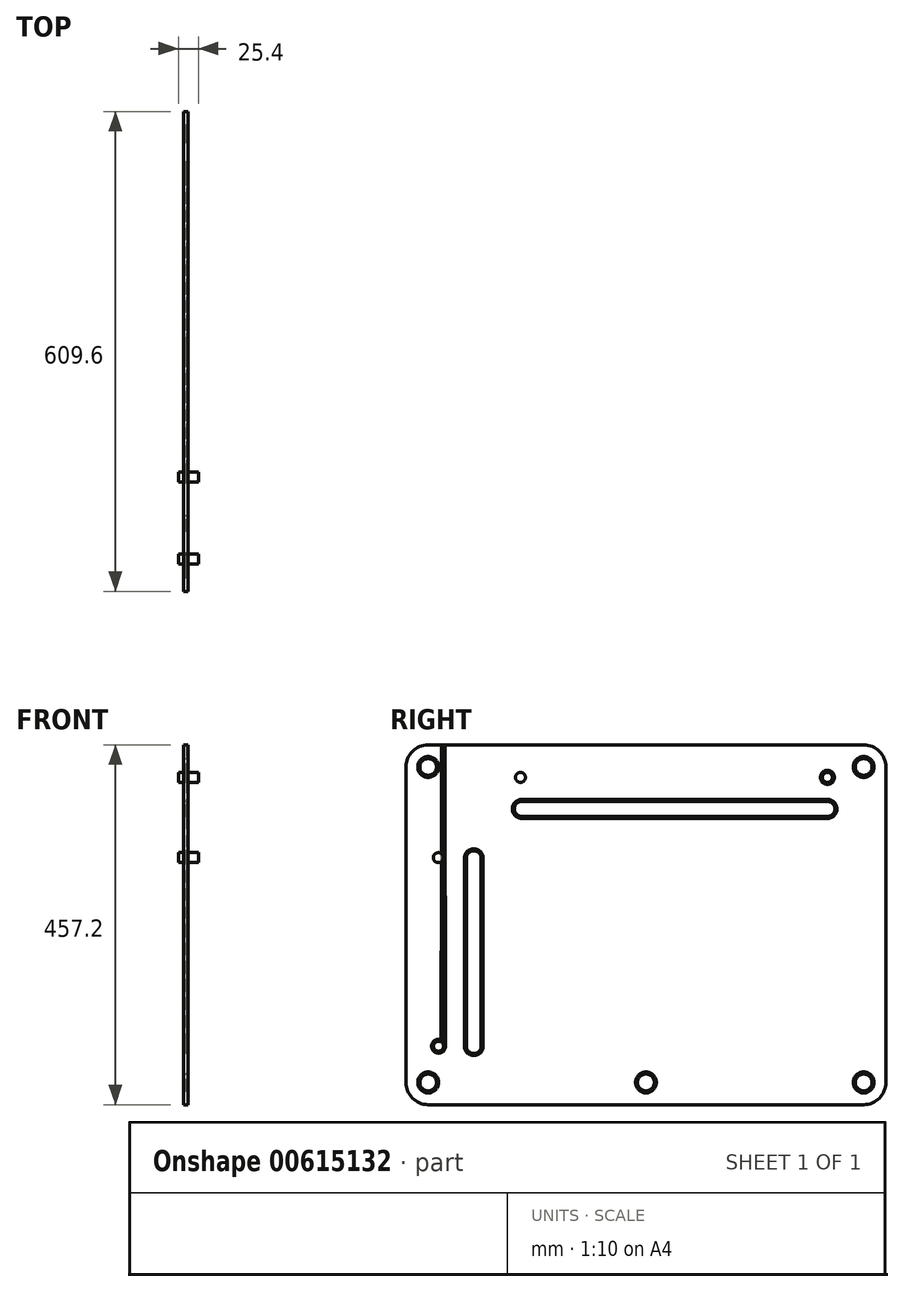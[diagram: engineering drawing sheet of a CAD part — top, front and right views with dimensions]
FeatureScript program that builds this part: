
annotation { "Feature Type Name" : "Feature", "Feature Type Description" : "" }
export const myFeature = defineFeature(function(context is Context, id is Id, definition is map)
    precondition{}
    {
        {
            var Q0;
            Q0=qCreatedBy(makeId("Right.planeOp"),FACE);
            var sketch = newSketch(context, id + "F0", { "sketchPlane" : qUnion([Q0])});
            skPoint(sketch, "E0.middle", {"position": v(0, 0) * mm});
            skLineSegment(sketch, "E1.bottom", {"start": v(304.8, -228.6) * mm, "end": v(-304.8, -228.6) * mm});
            skLineSegment(sketch, "E1.top", {"start": v(304.8, 228.6) * mm, "end": v(-304.8, 228.6) * mm});
            skLineSegment(sketch, "E1.left", {"start": v(304.8, -228.6) * mm, "end": v(304.8, 228.6) * mm});
            skLineSegment(sketch, "E1.right", {"start": v(-304.8, -228.6) * mm, "end": v(-304.8, 228.6) * mm});
            skSolve(sketch);
        }
        {
            var Q0;
            Q0=makeQuery(id+"F0.imprint","IMPRINT",FACE,{"disambiguationData":[TD([[makeQuery(id+"F0.imprint","IMPRINT",EDGE,{"derivedFrom":sQuery(id+"F0.wireOp",EDGE,"E1.bottom")}),-1.0]])]});
            extrude(context, id + "F1", {"entities" : qUnion([Q0]), "depth" : 6.35 * mm, "offsetDistance" : 25.4 * mm});
        }
        {
            var Q0;
            Q0=makeQuery(id+"F1.opExtrude","SWEPT_EDGE",EDGE,{"disambiguationData":[OSD([sQuery(id+"F0.wireOp",EDGE,"E1.top"),sQuery(id+"F0.wireOp",EDGE,"E1.right")])]});
            var Q1;
            Q1=makeQuery(id+"F1.opExtrude","SWEPT_EDGE",EDGE,{"disambiguationData":[OSD([sQuery(id+"F0.wireOp",EDGE,"E1.top"),sQuery(id+"F0.wireOp",EDGE,"E1.left")])]});
            var Q2;
            Q2=makeQuery(id+"F1.opExtrude","SWEPT_EDGE",EDGE,{"disambiguationData":[OSD([sQuery(id+"F0.wireOp",EDGE,"E1.bottom"),sQuery(id+"F0.wireOp",EDGE,"E1.right")])]});
            var Q3;
            Q3=makeQuery(id+"F1.opExtrude","SWEPT_EDGE",EDGE,{"disambiguationData":[OSD([sQuery(id+"F0.wireOp",EDGE,"E1.bottom"),sQuery(id+"F0.wireOp",EDGE,"E1.left")])]});
            fillet(context, id + "F2", {"entities" : qUnion([Q0, Q1, Q2, Q3]), "radius" : 28.2 * mm, "tangentPropagation" : true, "allowEdgeOverflow" : false});
        }
        {
            var Q0;
            Q0=makeQuery(id+"F1.opExtrude","CAP_FACE",FACE,{"disambiguationData":[OSD([sQuery(id+"F0.wireOp",EDGE,"E1.bottom"),sQuery(id+"F0.wireOp",EDGE,"E1.top"),sQuery(id+"F0.wireOp",EDGE,"E1.left"),sQuery(id+"F0.wireOp",EDGE,"E1.right")])],"isStart":true});
            var sketch = newSketch(context, id + "F3", { "sketchPlane" : qUnion([Q0])});
            skCircle(sketch, "E2", {"center": v(276.6, 200.4) * mm, "radius": 10.67 * mm});
            skCircle(sketch, "E3.MirrorC", {"center": v(-276.6, 200.4) * mm, "radius": 10.67 * mm});
            skCircle(sketch, "E4.MirrorC", {"center": v(276.6, -200.4) * mm, "radius": 10.67 * mm});
            skCircle(sketch, "E5.MirrorC", {"center": v(-276.6, -200.4) * mm, "radius": 10.67 * mm});
            skCircle(sketch, "E6", {"center": v(0, -200.4) * mm, "radius": 10.67 * mm});
            skSolve(sketch);
        }
        {
            var Q0;
            Q0 = qSketchRegion(id + "F3", true);
            extrude(context, id + "F4", {"entities" : qUnion([Q0]), "endBound" : BoundingType.SYMMETRIC, "depth" : 25.4 * mm, "offsetDistance" : 25.4 * mm});
        }
        {
            var Q0;
            Q0=makeQuery(id+"F4.opExtrude","SWEPT_BODY",BODY,{"disambiguationData":[OSD([sQuery(id+"F3.wireOp",EDGE,"E2")])]});
            var Q1;
            Q1=makeQuery(id+"F4.opExtrude","SWEPT_BODY",BODY,{"disambiguationData":[OSD([sQuery(id+"F3.wireOp",EDGE,"E3.MirrorC")])]});
            var Q2;
            Q2=makeQuery(id+"F4.opExtrude","SWEPT_BODY",BODY,{"disambiguationData":[OSD([sQuery(id+"F3.wireOp",EDGE,"E5.MirrorC")])]});
            var Q3;
            Q3=makeQuery(id+"F4.opExtrude","SWEPT_BODY",BODY,{"disambiguationData":[OSD([sQuery(id+"F3.wireOp",EDGE,"E6")])]});
            var Q4;
            Q4=makeQuery(id+"F4.opExtrude","SWEPT_BODY",BODY,{"disambiguationData":[OSD([sQuery(id+"F3.wireOp",EDGE,"E4.MirrorC")])]});
            var Q5;
            Q5=makeQuery(id+"F1.opExtrude","SWEPT_BODY",BODY,{"disambiguationData":[OSD([sQuery(id+"F0.wireOp",EDGE,"E1.bottom"),sQuery(id+"F0.wireOp",EDGE,"E1.top"),sQuery(id+"F0.wireOp",EDGE,"E1.left"),sQuery(id+"F0.wireOp",EDGE,"E1.right")])]});
            var Q6;
            Q6=makeQuery(id+"F1.opExtrude","SWEPT_BODY",BODY,{"disambiguationData":[OSD([sQuery(id+"F0.wireOp",EDGE,"E1.bottom"),sQuery(id+"F0.wireOp",EDGE,"E1.top"),sQuery(id+"F0.wireOp",EDGE,"E1.left"),sQuery(id+"F0.wireOp",EDGE,"E1.right")])]});
            booleanBodies(context, id + "F5", {"operationType" : BooleanOperationType.SUBTRACTION, "tools" : qUnion([Q0, Q1, Q2, Q3, Q4]), "targets" : qUnion([Q5, Q6])});
        }
        {
            var Q0;
            Q0=makeQuery(id+"F5.opBoolean","INTERSECT",EDGE,{"derivedFrom":[makeQuery(id+"F1.opExtrude","CAP_FACE",FACE,{"disambiguationData":[OSD([sQuery(id+"F0.wireOp",EDGE,"E1.bottom"),sQuery(id+"F0.wireOp",EDGE,"E1.top"),sQuery(id+"F0.wireOp",EDGE,"E1.left"),sQuery(id+"F0.wireOp",EDGE,"E1.right")])],"isStart":false}),makeQuery(id+"F4.opExtrude","SWEPT_FACE",FACE,{"disambiguationData":[OSD([sQuery(id+"F3.wireOp",EDGE,"E2")])]})]});
            var Q1;
            Q1=makeQuery(id+"F5.opBoolean","INTERSECT",EDGE,{"derivedFrom":[makeQuery(id+"F1.opExtrude","CAP_FACE",FACE,{"disambiguationData":[OSD([sQuery(id+"F0.wireOp",EDGE,"E1.bottom"),sQuery(id+"F0.wireOp",EDGE,"E1.top"),sQuery(id+"F0.wireOp",EDGE,"E1.left"),sQuery(id+"F0.wireOp",EDGE,"E1.right")])],"isStart":false}),makeQuery(id+"F4.opExtrude","SWEPT_FACE",FACE,{"disambiguationData":[OSD([sQuery(id+"F3.wireOp",EDGE,"E3.MirrorC")])]})]});
            var Q2;
            Q2=makeQuery(id+"F5.opBoolean","INTERSECT",EDGE,{"derivedFrom":[makeQuery(id+"F1.opExtrude","CAP_FACE",FACE,{"disambiguationData":[OSD([sQuery(id+"F0.wireOp",EDGE,"E1.bottom"),sQuery(id+"F0.wireOp",EDGE,"E1.top"),sQuery(id+"F0.wireOp",EDGE,"E1.left"),sQuery(id+"F0.wireOp",EDGE,"E1.right")])],"isStart":false}),makeQuery(id+"F4.opExtrude","SWEPT_FACE",FACE,{"disambiguationData":[OSD([sQuery(id+"F3.wireOp",EDGE,"E6")])]})]});
            var Q3;
            Q3=makeQuery(id+"F5.opBoolean","INTERSECT",EDGE,{"derivedFrom":[makeQuery(id+"F1.opExtrude","CAP_FACE",FACE,{"disambiguationData":[OSD([sQuery(id+"F0.wireOp",EDGE,"E1.bottom"),sQuery(id+"F0.wireOp",EDGE,"E1.top"),sQuery(id+"F0.wireOp",EDGE,"E1.left"),sQuery(id+"F0.wireOp",EDGE,"E1.right")])],"isStart":false}),makeQuery(id+"F4.opExtrude","SWEPT_FACE",FACE,{"disambiguationData":[OSD([sQuery(id+"F3.wireOp",EDGE,"E5.MirrorC")])]})]});
            var Q4;
            Q4=makeQuery(id+"F5.opBoolean","INTERSECT",EDGE,{"derivedFrom":[makeQuery(id+"F1.opExtrude","CAP_FACE",FACE,{"disambiguationData":[OSD([sQuery(id+"F0.wireOp",EDGE,"E1.bottom"),sQuery(id+"F0.wireOp",EDGE,"E1.top"),sQuery(id+"F0.wireOp",EDGE,"E1.left"),sQuery(id+"F0.wireOp",EDGE,"E1.right")])],"isStart":false}),makeQuery(id+"F4.opExtrude","SWEPT_FACE",FACE,{"disambiguationData":[OSD([sQuery(id+"F3.wireOp",EDGE,"E4.MirrorC")])]})]});
            chamfer(context, id + "F6", {"entities" : qUnion([Q0, Q1, Q2, Q3, Q4]), "width" : 2.54 * mm, "tangentPropagation" : true});
        }
        {
            var Q0;
            Q0=makeQuery(id+"F1.opExtrude","CAP_FACE",FACE,{"disambiguationData":[OSD([sQuery(id+"F0.wireOp",EDGE,"E1.bottom"),sQuery(id+"F0.wireOp",EDGE,"E1.top"),sQuery(id+"F0.wireOp",EDGE,"E1.left"),sQuery(id+"F0.wireOp",EDGE,"E1.right")])],"isStart":false});
            var sketch = newSketch(context, id + "F7", { "sketchPlane" : qUnion([Q0])});
            skSolve(sketch);
        }
        {
            var Q0;
            Q0=makeQuery(id+"F1.opExtrude","CAP_FACE",FACE,{"disambiguationData":[OSD([sQuery(id+"F0.wireOp",EDGE,"E1.bottom"),sQuery(id+"F0.wireOp",EDGE,"E1.top"),sQuery(id+"F0.wireOp",EDGE,"E1.left"),sQuery(id+"F0.wireOp",EDGE,"E1.right")])],"isStart":false});
            var sketch = newSketch(context, id + "F8", { "sketchPlane" : qUnion([Q0])});
            skLineSegment(sketch, "E7", {"start": v(-230.16, 193.53) * mm, "end": v(117.73, 193.53) * mm});
            skLineSegment(sketch, "E8", {"start": v(-230.5, 180.84) * mm, "end": v(159.64, 180.84) * mm});
            skLineSegment(sketch, "E9.MirrorCS", {"start": v(-257.1, 154.28) * mm, "end": v(-257.64, -235.87) * mm});
            skLineSegment(sketch, "E10.MirrorCS", {"start": v(-269.8, 153.95) * mm, "end": v(-270.27, -193.94) * mm});
            skLineSegment(sketch, "E11.MirrorCS", {"start": v(230.5, 180.84) * mm, "end": v(-159.64, 180.84) * mm});
            skLineSegment(sketch, "E12.MirrorCS", {"start": v(230.16, 193.53) * mm, "end": v(-117.73, 193.53) * mm});
            skCircle(sketch, "E13.MirrorC", {"center": v(230.5, 187.2) * mm, "radius": 6.35 * mm});
            skCircle(sketch, "E14.MirrorC", {"center": v(-263.45, -154.29) * mm, "radius": 6.35 * mm});
            skLineSegment(sketch, "E15.MirrorCS", {"start": v(-257.1, -154.28) * mm, "end": v(-257.64, 235.87) * mm});
            skLineSegment(sketch, "E16.MirrorCS", {"start": v(-269.8, -153.95) * mm, "end": v(-270.27, 193.94) * mm});
            skCircle(sketch, "E17", {"center": v(-159.4, 187.19) * mm, "radius": 6.35 * mm});
            skPoint(sketch, "E17.second.point", {"position": v(-159.64, 193.53) * mm});
            skPoint(sketch, "E17.third.point", {"position": v(-165.6, 185.8) * mm});
            skPoint(sketch, "E18.first.point", {"position": v(-270.12, 81.94) * mm});
            skPoint(sketch, "E18.second.point", {"position": v(-257.43, 81.94) * mm});
            skPoint(sketch, "E18.third.point", {"position": v(-257.43, 81.39) * mm});
            skCircle(sketch, "E19", {"center": v(-263.77, 85.22) * mm, "radius": 6.35 * mm});
            skPoint(sketch, "E19.first.point", {"position": v(-257.43, 85.64) * mm});
            skPoint(sketch, "E19.second.point", {"position": v(-270.12, 85.12) * mm});
            skPoint(sketch, "E19.third.point", {"position": v(-262.85, 78.93) * mm});
            skSolve(sketch);
        }
        {
            var Q0;
            Q0 = qSketchRegion(id + "F8", true);
            extrude(context, id + "F9", {"entities" : qUnion([Q0]), "endBound" : BoundingType.SYMMETRIC, "depth" : 25.4 * mm, "offsetDistance" : 25.4 * mm});
        }
        {
            var Q0;
            Q0=makeQuery(id+"F9.opExtrude","SWEPT_BODY",BODY,{"disambiguationData":[OSD([sQuery(id+"F8.wireOp",EDGE,"JYx8LGtQ-4H3j-zVlU-k91Q-ysmHY4vAFXg0"),sQuery(id+"F8.wireOp",EDGE,"E7"),sQuery(id+"F8.wireOp",EDGE,"E8"),sQuery(id+"F8.wireOp",EDGE,"E11.MirrorCS"),sQuery(id+"F8.wireOp",EDGE,"E12.MirrorCS"),sQuery(id+"F8.wireOp",EDGE,"E13.MirrorC")])]});
            var Q1;
            Q1=makeQuery(id+"F9.opExtrude","SWEPT_BODY",BODY,{"disambiguationData":[OSD([sQuery(id+"F8.wireOp",EDGE,"E9.MirrorCS"),sQuery(id+"F8.wireOp",EDGE,"2af65969-cf82-4882-8e88-bc3bc080c73c0.MirrorC"),sQuery(id+"F8.wireOp",EDGE,"E10.MirrorCS"),sQuery(id+"F8.wireOp",EDGE,"E14.MirrorC"),sQuery(id+"F8.wireOp",EDGE,"E16.MirrorCS"),sQuery(id+"F8.wireOp",EDGE,"E15.MirrorCS")])]});
            var Q2;
            Q2=makeQuery(id+"F1.opExtrude","SWEPT_BODY",BODY,{"disambiguationData":[OSD([sQuery(id+"F0.wireOp",EDGE,"E1.bottom"),sQuery(id+"F0.wireOp",EDGE,"E1.top"),sQuery(id+"F0.wireOp",EDGE,"E1.left"),sQuery(id+"F0.wireOp",EDGE,"E1.right")])]});
            booleanBodies(context, id + "F10", {"operationType" : BooleanOperationType.SUBTRACTION, "tools" : qUnion([Q0, Q1]), "targets" : qUnion([Q2])});
        }
        {
            var Q0;
            Q0=makeQuery(id+"F10.opBoolean","INTERSECT",EDGE,{"derivedFrom":[makeQuery(id+"F1.opExtrude","CAP_FACE",FACE,{"disambiguationData":[OSD([sQuery(id+"F0.wireOp",EDGE,"E1.bottom"),sQuery(id+"F0.wireOp",EDGE,"E1.top"),sQuery(id+"F0.wireOp",EDGE,"E1.left"),sQuery(id+"F0.wireOp",EDGE,"E1.right")])],"isStart":false}),makeQuery(id+"F9.opExtrude","SWEPT_FACE",FACE,{"disambiguationData":[OSD([sQuery(id+"F8.wireOp",EDGE,"E16.MirrorCS")])]})]});
            var Q1;
            Q1=makeQuery(id+"F10.opBoolean","INTERSECT",EDGE,{"derivedFrom":[makeQuery(id+"F1.opExtrude","CAP_FACE",FACE,{"disambiguationData":[OSD([sQuery(id+"F0.wireOp",EDGE,"E1.bottom"),sQuery(id+"F0.wireOp",EDGE,"E1.top"),sQuery(id+"F0.wireOp",EDGE,"E1.left"),sQuery(id+"F0.wireOp",EDGE,"E1.right")])],"isStart":false}),makeQuery(id+"F9.opExtrude","SWEPT_FACE",FACE,{"disambiguationData":[OSD([sQuery(id+"F8.wireOp",EDGE,"E10.MirrorCS")])]})]});
            var Q2;
            Q2=makeQuery(id+"F10.opBoolean","INTERSECT",EDGE,{"derivedFrom":[makeQuery(id+"F1.opExtrude","CAP_FACE",FACE,{"disambiguationData":[OSD([sQuery(id+"F0.wireOp",EDGE,"E1.bottom"),sQuery(id+"F0.wireOp",EDGE,"E1.top"),sQuery(id+"F0.wireOp",EDGE,"E1.left"),sQuery(id+"F0.wireOp",EDGE,"E1.right")])],"isStart":false}),makeQuery(id+"F9.opExtrude","SWEPT_FACE",FACE,{"disambiguationData":[OSD([sQuery(id+"F8.wireOp",EDGE,"E15.MirrorCS")])]})]});
            var Q3;
            Q3=makeQuery(id+"F10.opBoolean","INTERSECT",EDGE,{"derivedFrom":[makeQuery(id+"F1.opExtrude","CAP_FACE",FACE,{"disambiguationData":[OSD([sQuery(id+"F0.wireOp",EDGE,"E1.bottom"),sQuery(id+"F0.wireOp",EDGE,"E1.top"),sQuery(id+"F0.wireOp",EDGE,"E1.left"),sQuery(id+"F0.wireOp",EDGE,"E1.right")])],"isStart":false}),makeQuery(id+"F9.opExtrude","SWEPT_FACE",FACE,{"disambiguationData":[OSD([sQuery(id+"F8.wireOp",EDGE,"E9.MirrorCS")])]})]});
            var Q4;
            Q4=makeQuery(id+"F10.opBoolean","INTERSECT",EDGE,{"derivedFrom":[makeQuery(id+"F1.opExtrude","CAP_FACE",FACE,{"disambiguationData":[OSD([sQuery(id+"F0.wireOp",EDGE,"E1.bottom"),sQuery(id+"F0.wireOp",EDGE,"E1.top"),sQuery(id+"F0.wireOp",EDGE,"E1.left"),sQuery(id+"F0.wireOp",EDGE,"E1.right")])],"isStart":false}),makeQuery(id+"F9.opExtrude","SWEPT_FACE",FACE,{"disambiguationData":[OSD([sQuery(id+"F8.wireOp",EDGE,"E14.MirrorC")])]})]});
            var Q5;
            Q5=makeQuery(id+"F10.opBoolean","INTERSECT",EDGE,{"derivedFrom":[makeQuery(id+"F1.opExtrude","CAP_FACE",FACE,{"disambiguationData":[OSD([sQuery(id+"F0.wireOp",EDGE,"E1.bottom"),sQuery(id+"F0.wireOp",EDGE,"E1.top"),sQuery(id+"F0.wireOp",EDGE,"E1.left"),sQuery(id+"F0.wireOp",EDGE,"E1.right")])],"isStart":false}),makeQuery(id+"F9.opExtrude","SWEPT_FACE",FACE,{"disambiguationData":[OSD([sQuery(id+"F8.wireOp",EDGE,"2af65969-cf82-4882-8e88-bc3bc080c73c0.MirrorC")])]})]});
            var Q6;
            Q6=makeQuery(id+"F10.opBoolean","INTERSECT",EDGE,{"derivedFrom":[makeQuery(id+"F1.opExtrude","CAP_FACE",FACE,{"disambiguationData":[OSD([sQuery(id+"F0.wireOp",EDGE,"E1.bottom"),sQuery(id+"F0.wireOp",EDGE,"E1.top"),sQuery(id+"F0.wireOp",EDGE,"E1.left"),sQuery(id+"F0.wireOp",EDGE,"E1.right")])],"isStart":false}),makeQuery(id+"F9.opExtrude","SWEPT_FACE",FACE,{"disambiguationData":[OSD([sQuery(id+"F8.wireOp",EDGE,"E8"),sQuery(id+"F8.wireOp",EDGE,"E11.MirrorCS")])]})]});
            var Q7;
            Q7=makeQuery(id+"F10.opBoolean","INTERSECT",EDGE,{"derivedFrom":[makeQuery(id+"F1.opExtrude","CAP_FACE",FACE,{"disambiguationData":[OSD([sQuery(id+"F0.wireOp",EDGE,"E1.bottom"),sQuery(id+"F0.wireOp",EDGE,"E1.top"),sQuery(id+"F0.wireOp",EDGE,"E1.left"),sQuery(id+"F0.wireOp",EDGE,"E1.right")])],"isStart":false}),makeQuery(id+"F9.opExtrude","SWEPT_FACE",FACE,{"disambiguationData":[OSD([sQuery(id+"F8.wireOp",EDGE,"E7"),sQuery(id+"F8.wireOp",EDGE,"E12.MirrorCS")])]})]});
            var Q8;
            Q8=makeQuery(id+"F10.opBoolean","INTERSECT",EDGE,{"derivedFrom":[makeQuery(id+"F1.opExtrude","CAP_FACE",FACE,{"disambiguationData":[OSD([sQuery(id+"F0.wireOp",EDGE,"E1.bottom"),sQuery(id+"F0.wireOp",EDGE,"E1.top"),sQuery(id+"F0.wireOp",EDGE,"E1.left"),sQuery(id+"F0.wireOp",EDGE,"E1.right")])],"isStart":false}),makeQuery(id+"F9.opExtrude","SWEPT_FACE",FACE,{"disambiguationData":[OSD([sQuery(id+"F8.wireOp",EDGE,"JYx8LGtQ-4H3j-zVlU-k91Q-ysmHY4vAFXg0")])]})]});
            var Q9;
            Q9=makeQuery(id+"F10.opBoolean","INTERSECT",EDGE,{"derivedFrom":[makeQuery(id+"F1.opExtrude","CAP_FACE",FACE,{"disambiguationData":[OSD([sQuery(id+"F0.wireOp",EDGE,"E1.bottom"),sQuery(id+"F0.wireOp",EDGE,"E1.top"),sQuery(id+"F0.wireOp",EDGE,"E1.left"),sQuery(id+"F0.wireOp",EDGE,"E1.right")])],"isStart":false}),makeQuery(id+"F9.opExtrude","SWEPT_FACE",FACE,{"disambiguationData":[OSD([sQuery(id+"F8.wireOp",EDGE,"E13.MirrorC")])]})]});
            chamfer(context, id + "F11", {"entities" : qUnion([Q0, Q1, Q2, Q3, Q4, Q5, Q6, Q7, Q8, Q9]), "width" : 2.54 * mm, "tangentPropagation" : true});
        }
        {
            var Q0;
            {var subQ3=sQuery(id+"F0.wireOp",EDGE,"E1.bottom");Q0=makeQuery(id+"F7.imprint","IMPRINT",FACE,{"disambiguationData":[TD([[makeQuery(id+"F7.imprint","IMPRINT",EDGE,{"derivedFrom":makeQuery(id+"F1.opExtrude","CAP_EDGE",EDGE,{"disambiguationData":[OSD([subQ3])],"isStart":false})}),-1.0]])]});}
            var sketch = newSketch(context, id + "F12", { "sketchPlane" : qUnion([Q0])});
            skLineSegment(sketch, "E20", {"start": v(230.59, 186.86) * mm, "end": v(230.59, 147.1) * mm});
            skCircle(sketch, "E21", {"center": v(230.59, 147.1) * mm, "radius": 9.53 * mm});
            skCircle(sketch, "E22", {"center": v(-157.7, 147.1) * mm, "radius": 9.53 * mm});
            skLineSegment(sketch, "E23", {"start": v(230.59, 147.1) * mm, "end": v(-157.7, 147.1) * mm});
            skLineSegment(sketch, "E24", {"start": v(-276.13, 201.1) * mm, "end": v(-69.15, 0) * mm});
            skCircle(sketch, "E25.MirrorC", {"center": v(-218.73, 84.28) * mm, "radius": 9.53 * mm});
            skCircle(sketch, "E26", {"center": v(-218.73, -154.1) * mm, "radius": 9.53 * mm});
            skLineSegment(sketch, "E27", {"start": v(-157.7, 156.62) * mm, "end": v(230.59, 156.62) * mm});
            skLineSegment(sketch, "E28", {"start": v(230.59, 137.57) * mm, "end": v(-157.7, 137.57) * mm});
            skLineSegment(sketch, "E29", {"start": v(-228.26, 84.28) * mm, "end": v(-228.26, -154.1) * mm});
            skLineSegment(sketch, "E30", {"start": v(-209.25, -155.01) * mm, "end": v(-209.25, 84.28) * mm});
            skSolve(sketch);
        }
        {
            var Q0;
            Q0 = qSketchRegion(id + "F12", true);
            extrude(context, id + "F13", {"entities" : qUnion([Q0]), "endBound" : BoundingType.SYMMETRIC, "depth" : 25.4 * mm, "offsetDistance" : 25.4 * mm});
        }
        {
            var Q0;
            Q0=makeQuery(id+"F13.opExtrude","SWEPT_BODY",BODY,{"disambiguationData":[OSD([sQuery(id+"F12.wireOp",EDGE,"E25.MirrorC"),sQuery(id+"F12.wireOp",EDGE,"E26"),sQuery(id+"F12.wireOp",EDGE,"E29"),sQuery(id+"F12.wireOp",EDGE,"E30")])]});
            var Q1;
            Q1=makeQuery(id+"F13.opExtrude","SWEPT_BODY",BODY,{"disambiguationData":[OSD([sQuery(id+"F12.wireOp",EDGE,"E21"),sQuery(id+"F12.wireOp",EDGE,"E22"),sQuery(id+"F12.wireOp",EDGE,"E27"),sQuery(id+"F12.wireOp",EDGE,"E28")])]});
            var Q2;
            Q2=makeQuery(id+"F1.opExtrude","SWEPT_BODY",BODY,{"disambiguationData":[OSD([sQuery(id+"F0.wireOp",EDGE,"E1.bottom"),sQuery(id+"F0.wireOp",EDGE,"E1.top"),sQuery(id+"F0.wireOp",EDGE,"E1.left"),sQuery(id+"F0.wireOp",EDGE,"E1.right")])]});
            booleanBodies(context, id + "F14", {"operationType" : BooleanOperationType.SUBTRACTION, "tools" : qUnion([Q0, Q1]), "targets" : qUnion([Q2])});
        }
        {
            var Q0;
            Q0=makeQuery(id+"F14.opBoolean","INTERSECT",EDGE,{"derivedFrom":[makeQuery(id+"F1.opExtrude","CAP_FACE",FACE,{"disambiguationData":[OSD([sQuery(id+"F0.wireOp",EDGE,"E1.bottom"),sQuery(id+"F0.wireOp",EDGE,"E1.top"),sQuery(id+"F0.wireOp",EDGE,"E1.left"),sQuery(id+"F0.wireOp",EDGE,"E1.right")])],"isStart":false}),makeQuery(id+"F13.opExtrude","SWEPT_FACE",FACE,{"disambiguationData":[OSD([sQuery(id+"F12.wireOp",EDGE,"E27")])]})]});
            var Q1;
            Q1=makeQuery(id+"F14.opBoolean","INTERSECT",EDGE,{"derivedFrom":[makeQuery(id+"F1.opExtrude","CAP_FACE",FACE,{"disambiguationData":[OSD([sQuery(id+"F0.wireOp",EDGE,"E1.bottom"),sQuery(id+"F0.wireOp",EDGE,"E1.top"),sQuery(id+"F0.wireOp",EDGE,"E1.left"),sQuery(id+"F0.wireOp",EDGE,"E1.right")])],"isStart":false}),makeQuery(id+"F13.opExtrude","SWEPT_FACE",FACE,{"disambiguationData":[OSD([sQuery(id+"F12.wireOp",EDGE,"E28")])]})]});
            var Q2;
            Q2=makeQuery(id+"F14.opBoolean","INTERSECT",EDGE,{"derivedFrom":[makeQuery(id+"F1.opExtrude","CAP_FACE",FACE,{"disambiguationData":[OSD([sQuery(id+"F0.wireOp",EDGE,"E1.bottom"),sQuery(id+"F0.wireOp",EDGE,"E1.top"),sQuery(id+"F0.wireOp",EDGE,"E1.left"),sQuery(id+"F0.wireOp",EDGE,"E1.right")])],"isStart":false}),makeQuery(id+"F13.opExtrude","SWEPT_FACE",FACE,{"disambiguationData":[OSD([sQuery(id+"F12.wireOp",EDGE,"E22")])]})]});
            var Q3;
            Q3=makeQuery(id+"F14.opBoolean","INTERSECT",EDGE,{"derivedFrom":[makeQuery(id+"F1.opExtrude","CAP_FACE",FACE,{"disambiguationData":[OSD([sQuery(id+"F0.wireOp",EDGE,"E1.bottom"),sQuery(id+"F0.wireOp",EDGE,"E1.top"),sQuery(id+"F0.wireOp",EDGE,"E1.left"),sQuery(id+"F0.wireOp",EDGE,"E1.right")])],"isStart":false}),makeQuery(id+"F13.opExtrude","SWEPT_FACE",FACE,{"disambiguationData":[OSD([sQuery(id+"F12.wireOp",EDGE,"E21")])]})]});
            var Q4;
            Q4=makeQuery(id+"F14.opBoolean","INTERSECT",EDGE,{"derivedFrom":[makeQuery(id+"F1.opExtrude","CAP_FACE",FACE,{"disambiguationData":[OSD([sQuery(id+"F0.wireOp",EDGE,"E1.bottom"),sQuery(id+"F0.wireOp",EDGE,"E1.top"),sQuery(id+"F0.wireOp",EDGE,"E1.left"),sQuery(id+"F0.wireOp",EDGE,"E1.right")])],"isStart":false}),makeQuery(id+"F13.opExtrude","SWEPT_FACE",FACE,{"disambiguationData":[OSD([sQuery(id+"F12.wireOp",EDGE,"E25.MirrorC")])]})]});
            var Q5;
            Q5=makeQuery(id+"F14.opBoolean","INTERSECT",EDGE,{"derivedFrom":[makeQuery(id+"F1.opExtrude","CAP_FACE",FACE,{"disambiguationData":[OSD([sQuery(id+"F0.wireOp",EDGE,"E1.bottom"),sQuery(id+"F0.wireOp",EDGE,"E1.top"),sQuery(id+"F0.wireOp",EDGE,"E1.left"),sQuery(id+"F0.wireOp",EDGE,"E1.right")])],"isStart":false}),makeQuery(id+"F13.opExtrude","SWEPT_FACE",FACE,{"disambiguationData":[OSD([sQuery(id+"F12.wireOp",EDGE,"E30")])]})]});
            var Q6;
            Q6=makeQuery(id+"F14.opBoolean","INTERSECT",EDGE,{"derivedFrom":[makeQuery(id+"F1.opExtrude","CAP_FACE",FACE,{"disambiguationData":[OSD([sQuery(id+"F0.wireOp",EDGE,"E1.bottom"),sQuery(id+"F0.wireOp",EDGE,"E1.top"),sQuery(id+"F0.wireOp",EDGE,"E1.left"),sQuery(id+"F0.wireOp",EDGE,"E1.right")])],"isStart":false}),makeQuery(id+"F13.opExtrude","SWEPT_FACE",FACE,{"disambiguationData":[OSD([sQuery(id+"F12.wireOp",EDGE,"E29")])]})]});
            var Q7;
            Q7=makeQuery(id+"F14.opBoolean","INTERSECT",EDGE,{"derivedFrom":[makeQuery(id+"F1.opExtrude","CAP_FACE",FACE,{"disambiguationData":[OSD([sQuery(id+"F0.wireOp",EDGE,"E1.bottom"),sQuery(id+"F0.wireOp",EDGE,"E1.top"),sQuery(id+"F0.wireOp",EDGE,"E1.left"),sQuery(id+"F0.wireOp",EDGE,"E1.right")])],"isStart":false}),makeQuery(id+"F13.opExtrude","SWEPT_FACE",FACE,{"disambiguationData":[OSD([sQuery(id+"F12.wireOp",EDGE,"E26")])]})]});
            chamfer(context, id + "F15", {"entities" : qUnion([Q0, Q1, Q2, Q3, Q4, Q5, Q6, Q7]), "width" : 2.54 * mm, "tangentPropagation" : true});
        }
    });
